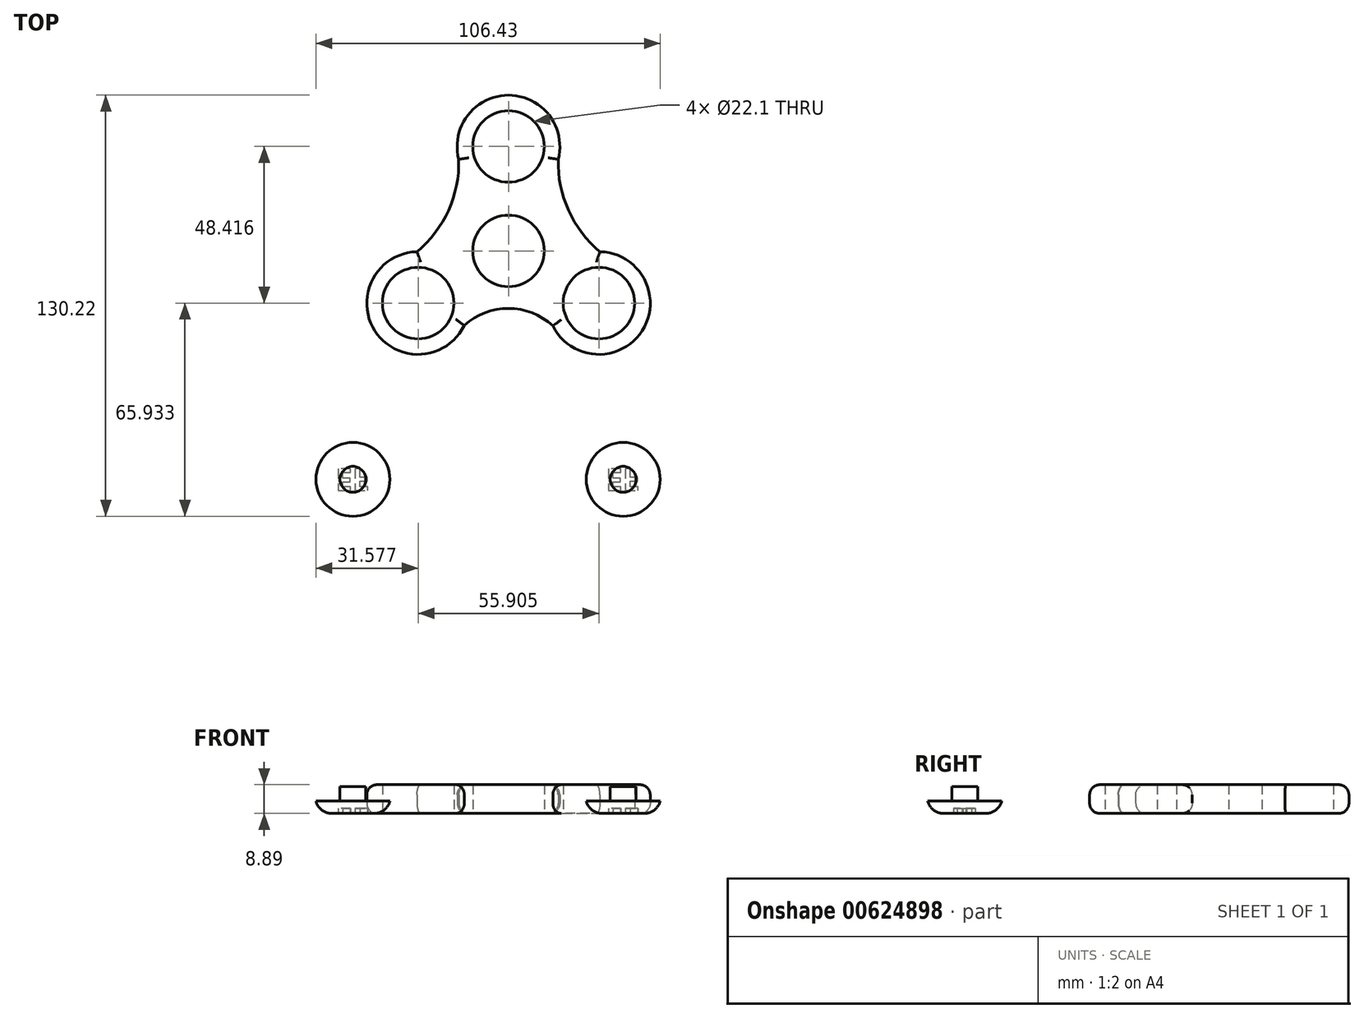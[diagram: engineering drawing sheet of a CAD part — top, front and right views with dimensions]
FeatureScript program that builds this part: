
annotation { "Feature Type Name" : "Feature", "Feature Type Description" : "" }
export const myFeature = defineFeature(function(context is Context, id is Id, definition is map)
    precondition{}
    {
        {
            var Q0;
            Q0=qCreatedBy(makeId("Top.planeOp"),FACE);
            var sketch = newSketch(context, id + "F0", { "sketchPlane" : qUnion([Q0])});
            skCircle(sketch, "E0", {"center": v(0, 59.7) * mm, "radius": 11.05 * mm});
            skCircle(sketch, "E1.1.0", {"center": v(-27.95, 11.3) * mm, "radius": 11.05 * mm});
            skCircle(sketch, "E1.2.0", {"center": v(27.95, 11.3) * mm, "radius": 11.05 * mm});
            skPoint(sketch, "E1.center", {"position": v(0, 27.43) * mm});
            skCircle(sketch, "E2", {"center": v(0, 27.43) * mm, "radius": 11.05 * mm});
            skArc(sketch, "E3", {"start": v(15.38, 55.77) * mm, "mid": v(0, 75.58) * mm, "end": v(-15.38, 55.77) * mm});
            skArc(sketch, "E4", {"start": v(-28.28, 27.17) * mm, "mid": v(-41.32, 2.73) * mm, "end": v(-13.67, 4.36) * mm});
            skArc(sketch, "E5", {"start": v(13.72, 4.25) * mm, "mid": v(41.35, 2.78) * mm, "end": v(28.28, 27.17) * mm});
            skArc(sketch, "E6", {"start": v(-28.28, 27.17) * mm, "mid": v(-17.61, 42.26) * mm, "end": v(-15.85, 60.66) * mm});
            skArc(sketch, "E7.MirrorCS", {"start": v(28.28, 27.17) * mm, "mid": v(17.61, 42.26) * mm, "end": v(15.85, 60.66) * mm});
            skArc(sketch, "E8", {"start": v(13.72, 4.25) * mm, "mid": v(0.05, 9.65) * mm, "end": v(-13.67, 4.36) * mm});
            skSolve(sketch);
        }
        {
            var Q0;
            Q0 = qSketchRegion(id + "F0", true);
            extrude(context, id + "F1", {"entities" : qUnion([Q0]), "depth" : 8.9 * mm, "offsetDistance" : 25.4 * mm});
        }
        {
            var Q0;
            Q0=makeQuery(id+"F1.opExtrude","CAP_EDGE",EDGE,{"disambiguationData":[OSD([sQuery(id+"F0.wireOp",EDGE,"E4")])],"isStart":false});
            var Q1;
            Q1=makeQuery(id+"F1.opExtrude","CAP_EDGE",EDGE,{"disambiguationData":[OSD([sQuery(id+"F0.wireOp",EDGE,"E5")])],"isStart":false});
            var Q2;
            Q2=makeQuery(id+"F1.opExtrude","CAP_EDGE",EDGE,{"disambiguationData":[OSD([sQuery(id+"F0.wireOp",EDGE,"E8")])],"isStart":false});
            var Q3;
            Q3=makeQuery(id+"F1.opExtrude","CAP_EDGE",EDGE,{"disambiguationData":[OSD([sQuery(id+"F0.wireOp",EDGE,"E7.MirrorCS")])],"isStart":false});
            var Q4;
            Q4=makeQuery(id+"F1.opExtrude","CAP_EDGE",EDGE,{"disambiguationData":[OSD([sQuery(id+"F0.wireOp",EDGE,"E3")])],"isStart":false});
            var Q5;
            Q5=makeQuery(id+"F1.opExtrude","CAP_EDGE",EDGE,{"disambiguationData":[OSD([sQuery(id+"F0.wireOp",EDGE,"E6")])],"isStart":false});
            var Q6;
            Q6=makeQuery(id+"F1.opExtrude","CAP_EDGE",EDGE,{"disambiguationData":[OSD([sQuery(id+"F0.wireOp",EDGE,"E5")])],"isStart":true});
            var Q7;
            Q7=makeQuery(id+"F1.opExtrude","CAP_EDGE",EDGE,{"disambiguationData":[OSD([sQuery(id+"F0.wireOp",EDGE,"E8")])],"isStart":true});
            var Q8;
            Q8=makeQuery(id+"F1.opExtrude","CAP_EDGE",EDGE,{"disambiguationData":[OSD([sQuery(id+"F0.wireOp",EDGE,"E4")])],"isStart":true});
            var Q9;
            Q9=makeQuery(id+"F1.opExtrude","CAP_EDGE",EDGE,{"disambiguationData":[OSD([sQuery(id+"F0.wireOp",EDGE,"E7.MirrorCS")])],"isStart":true});
            var Q10;
            Q10=makeQuery(id+"F1.opExtrude","CAP_EDGE",EDGE,{"disambiguationData":[OSD([sQuery(id+"F0.wireOp",EDGE,"E3")])],"isStart":true});
            var Q11;
            Q11=makeQuery(id+"F1.opExtrude","CAP_EDGE",EDGE,{"disambiguationData":[OSD([sQuery(id+"F0.wireOp",EDGE,"E6")])],"isStart":true});
            fillet(context, id + "F2", {"entities" : qUnion([Q0, Q1, Q2, Q3, Q4, Q5, Q6, Q7, Q8, Q9, Q10, Q11]), "radius" : 3.17 * mm, "tangentPropagation" : true, "allowEdgeOverflow" : false});
        }
        {
            var Q0;
            Q0=qCreatedBy(makeId("Top.planeOp"),FACE);
            var sketch = newSketch(context, id + "F3", { "sketchPlane" : qUnion([Q0])});
            skCircle(sketch, "E9", {"center": v(-48.1, -43.21) * mm, "radius": 11.43 * mm});
            skSolve(sketch);
        }
        {
            var Q0;
            Q0=makeQuery(id+"F3.imprint","IMPRINT",FACE,{"disambiguationData":[TD([[makeQuery(id+"F3.imprint","IMPRINT",EDGE,{"derivedFrom":sQuery(id+"F3.wireOp",EDGE,"E9")}),1.0]])]});
            extrude(context, id + "F4", {"entities" : qUnion([Q0]), "depth" : 3.8 * mm, "offsetDistance" : 25.4 * mm});
        }
        {
            var Q0;
            Q0=makeQuery(id+"F4.opExtrude","CAP_FACE",FACE,{"disambiguationData":[OSD([sQuery(id+"F3.wireOp",EDGE,"E9")])],"isStart":false});
            var sketch = newSketch(context, id + "F5", { "sketchPlane" : qUnion([Q0])});
            skCircle(sketch, "E10", {"center": v(-48.1, -43.21) * mm, "radius": 4 * mm});
            skSolve(sketch);
        }
        {
            var Q0;
            Q0=makeQuery(id+"F5.imprint","IMPRINT",FACE,{"disambiguationData":[TD([[makeQuery(id+"F5.imprint","IMPRINT",EDGE,{"derivedFrom":sQuery(id+"F5.wireOp",EDGE,"E10")}),1.0]])]});
            extrude(context, id + "F6", {"entities" : qUnion([Q0]), "operationType" : NewBodyOperationType.ADD, "depth" : 4.44 * mm, "offsetDistance" : 25.4 * mm});
        }
        {
            var Q0;
            Q0=makeQuery(id+"F4.opExtrude","CAP_FACE",FACE,{"disambiguationData":[OSD([sQuery(id+"F3.wireOp",EDGE,"E9")])],"isStart":true});
            fillet(context, id + "F7", {"entities" : qUnion([Q0]), "radius" : 5.08 * mm, "tangentPropagation" : true, "allowEdgeOverflow" : false});
        }
        {
            var Q0;
            Q0=makeQuery(id+"F4.opExtrude","CAP_FACE",FACE,{"disambiguationData":[OSD([sQuery(id+"F3.wireOp",EDGE,"E9")])],"isStart":true});
            var sketch = newSketch(context, id + "F8", { "sketchPlane" : qUnion([Q0])});
            skText(sketch, "E11", { "text": "EF", "fontName": "OpenSans-Bold.ttf"});
            const initialGuessF8  = {"E11": [-0.05356, 0.03992, 1, 0, 0.00684]};
            skSetInitialGuess(sketch, initialGuessF8);
            skSolve(sketch);
        }
        {
            var Q0;
            Q0 = qSketchRegion(id + "F8", true);
            extrude(context, id + "F9", {"entities" : qUnion([Q0]), "operationType" : NewBodyOperationType.REMOVE, "oppositeDirection" : true, "depth" : 1.52 * mm, "offsetDistance" : 25.4 * mm});
        }
        {
            var Q0;
            Q0=makeQuery(id+"F4.opExtrude","SWEPT_BODY",BODY,{"disambiguationData":[OSD([sQuery(id+"F3.wireOp",EDGE,"E9")])]});
            transform(context, id + "F10", {"entities" : qUnion([Q0]), "transformType" : TransformType.TRANSLATION_3D, "dx" : 83.57 * mm, "dy" : 0 * mm, "dz" : 0 * mm, "makeCopy" : true});
        }
    });
